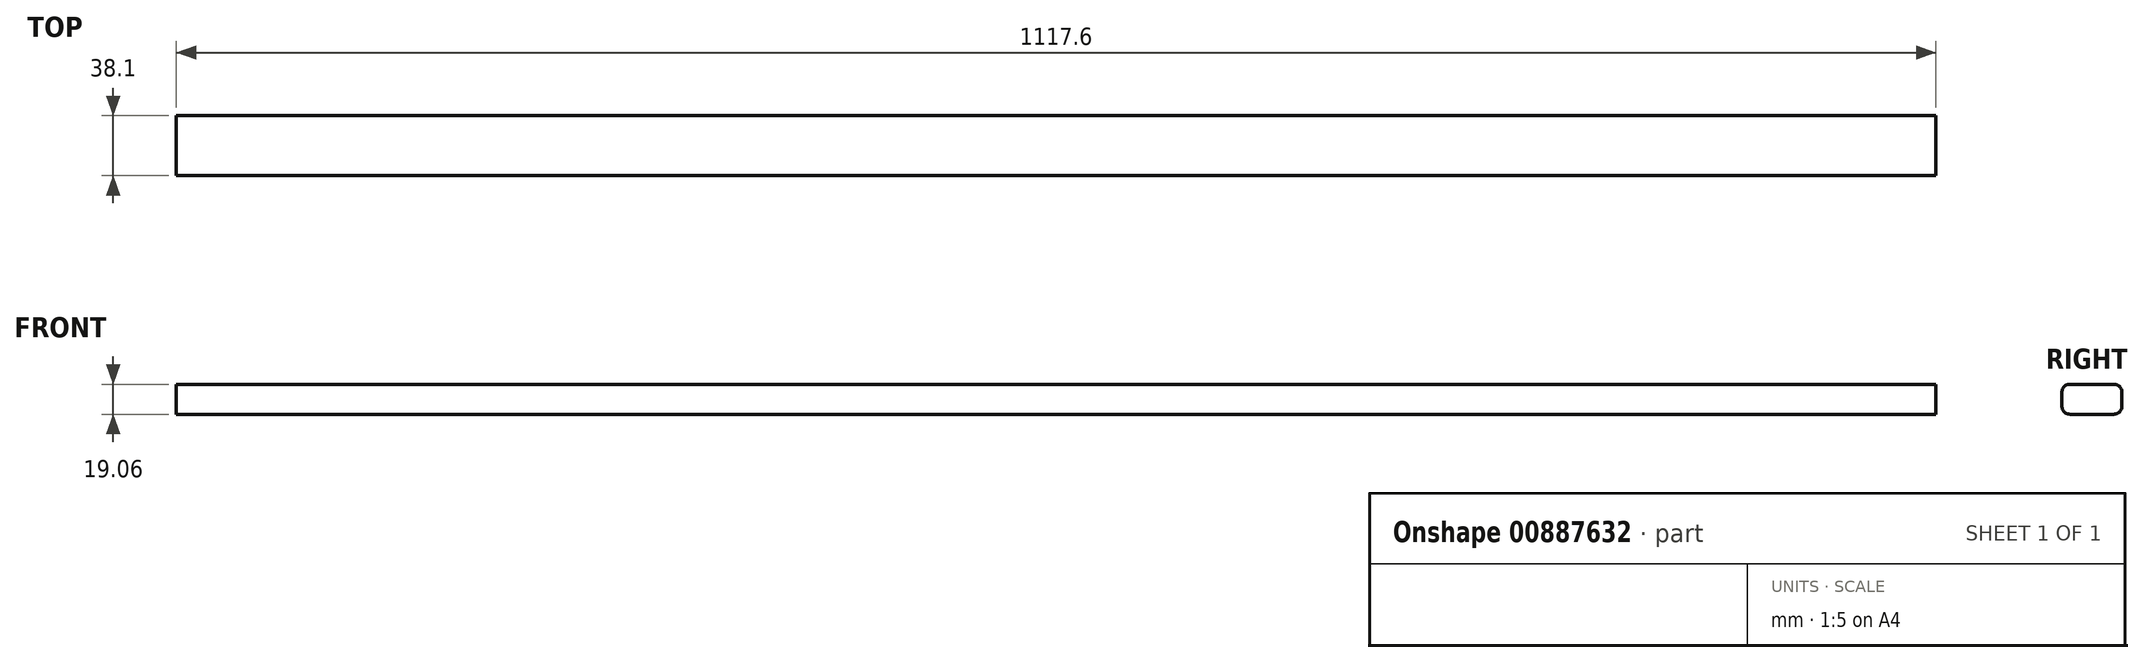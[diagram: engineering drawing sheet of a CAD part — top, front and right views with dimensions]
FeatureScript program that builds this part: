
annotation { "Feature Type Name" : "Feature", "Feature Type Description" : "" }
export const myFeature = defineFeature(function(context is Context, id is Id, definition is map)
    precondition{}
    {
        {
            var Q0;
            Q0=qCreatedBy(makeId("Right.planeOp"),FACE);
            var sketch = newSketch(context, id + "F0", { "sketchPlane" : qUnion([Q0])});
            skLineSegment(sketch, "E0.bottom", {"start": v(19.05, 9.52) * mm, "end": v(-19.05, 9.52) * mm});
            skLineSegment(sketch, "E0.top", {"start": v(19.05, -9.53) * mm, "end": v(-19.05, -9.53) * mm});
            skLineSegment(sketch, "E0.left", {"start": v(19.05, 9.52) * mm, "end": v(19.05, -9.53) * mm});
            skLineSegment(sketch, "E0.right", {"start": v(-19.05, 9.52) * mm, "end": v(-19.05, -9.53) * mm});
            skPoint(sketch, "E0.middle", {"position": v(0, 0) * mm});
            skSolve(sketch);
        }
        {
            var Q0;
            Q0=makeQuery(id+"F0.imprint","IMPRINT",FACE,{"disambiguationData":[TD([[makeQuery(id+"F0.imprint","IMPRINT",EDGE,{"derivedFrom":sQuery(id+"F0.wireOp",EDGE,"E0.bottom")}),1.0]])]});
            extrude(context, id + "F1", {"entities" : qUnion([Q0]), "endBound" : BoundingType.SYMMETRIC, "depth" : 1117.6 * mm, "offsetDistance" : 25.4 * mm});
        }
        {
            var Q0;
            Q0=makeQuery(id+"F1.opExtrude","SWEPT_EDGE",EDGE,{"disambiguationData":[OSD([sQuery(id+"F0.wireOp",EDGE,"E0.bottom"),sQuery(id+"F0.wireOp",EDGE,"E0.right")])]});
            var Q1;
            Q1=makeQuery(id+"F1.opExtrude","SWEPT_EDGE",EDGE,{"disambiguationData":[OSD([sQuery(id+"F0.wireOp",EDGE,"E0.top"),sQuery(id+"F0.wireOp",EDGE,"E0.right")])]});
            var Q2;
            Q2=makeQuery(id+"F1.opExtrude","SWEPT_EDGE",EDGE,{"disambiguationData":[OSD([sQuery(id+"F0.wireOp",EDGE,"E0.bottom"),sQuery(id+"F0.wireOp",EDGE,"E0.left")])]});
            var Q3;
            Q3=makeQuery(id+"F1.opExtrude","SWEPT_EDGE",EDGE,{"disambiguationData":[OSD([sQuery(id+"F0.wireOp",EDGE,"E0.top"),sQuery(id+"F0.wireOp",EDGE,"E0.left")])]});
            fillet(context, id + "F2", {"entities" : qUnion([Q0, Q1, Q2, Q3]), "radius" : 5.08 * mm, "tangentPropagation" : true, "allowEdgeOverflow" : false});
        }
    });
